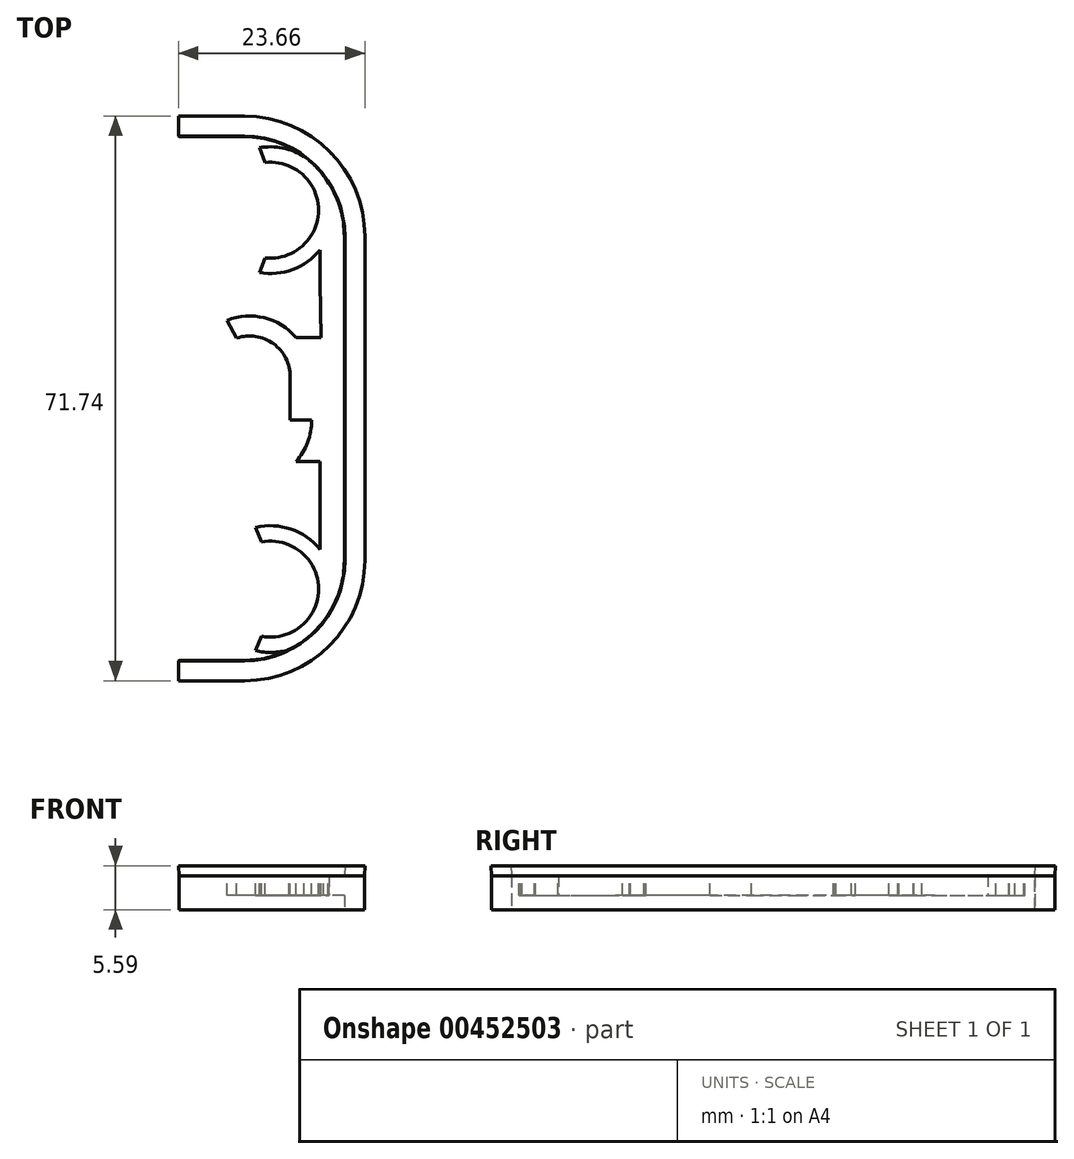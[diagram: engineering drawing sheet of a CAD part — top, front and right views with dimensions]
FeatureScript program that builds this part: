
annotation { "Feature Type Name" : "Feature", "Feature Type Description" : "" }
export const myFeature = defineFeature(function(context is Context, id is Id, definition is map)
    precondition{}
    {
        {
            var Q0;
            Q0=qCreatedBy(makeId("Top.planeOp"),FACE);
            var sketch = newSketch(context, id + "F0", { "sketchPlane" : qUnion([Q0])});
            skLineSegment(sketch, "E0", {"start": v(0, 0) * mm, "end": v(0, -66.52) * mm});
            skLineSegment(sketch, "E1", {"start": v(0, -66.52) * mm, "end": v(5.74, -66.52) * mm});
            skLineSegment(sketch, "E2", {"start": v(0, 0) * mm, "end": v(5.74, 0) * mm});
            skArc(sketch, "E3", {"start": v(5.74, 0) * mm, "mid": v(14.72, -3.72) * mm, "end": v(18.44, -12.7) * mm});
            skArc(sketch, "E4", {"start": v(5.74, -66.52) * mm, "mid": v(14.72, -62.8) * mm, "end": v(18.44, -53.82) * mm});
            skLineSegment(sketch, "E5", {"start": v(18.44, -12.7) * mm, "end": v(18.44, -53.82) * mm});
            skLineSegment(sketch, "E6.0", {"start": v(-2.54, 2.54) * mm, "end": v(5.74, 2.54) * mm});
            skLineSegment(sketch, "E6.1", {"start": v(20.98, -12.7) * mm, "end": v(20.98, -53.82) * mm});
            skArc(sketch, "E6.2", {"start": v(5.74, -69.06) * mm, "mid": v(16.52, -64.6) * mm, "end": v(20.98, -53.82) * mm});
            skArc(sketch, "E6.3", {"start": v(5.74, 2.54) * mm, "mid": v(16.52, -1.92) * mm, "end": v(20.98, -12.7) * mm});
            skLineSegment(sketch, "E6.4", {"start": v(-2.54, -69.06) * mm, "end": v(5.74, -69.06) * mm});
            skLineSegment(sketch, "E6.5", {"start": v(-2.54, 2.54) * mm, "end": v(-2.54, -69.06) * mm});
            skSolve(sketch);
        }
        {
            var Q0;
            Q0=makeQuery(id+"F0.imprint","IMPRINT",FACE,{"disambiguationData":[TD([[makeQuery(id+"F0.imprint","IMPRINT",EDGE,{"derivedFrom":sQuery(id+"F0.wireOp",EDGE,"E0")}),-1.0]])]});
            var Q1;
            Q1=makeQuery(id+"F0.imprint","IMPRINT",FACE,{"disambiguationData":[TD([[makeQuery(id+"F0.imprint","IMPRINT",EDGE,{"derivedFrom":sQuery(id+"F0.wireOp",EDGE,"E0")}),1.0]])]});
            extrude(context, id + "F1", {"entities" : qUnion([Q0, Q1]), "depth" : 1.27 * mm, "hasDraft" : true, "draftAngle" : 3 * degree, "hasSecondDirection" : true, "secondDirectionOppositeDirection" : true, "secondDirectionDepth" : 4.32 * mm});
        }
        {
            var Q0;
            Q0=makeQuery(id+"F1.opExtrude","CAP_FACE",FACE,{"disambiguationData":[OSD([sQuery(id+"F0.wireOp",EDGE,"E6.0"),sQuery(id+"F0.wireOp",EDGE,"E6.1"),sQuery(id+"F0.wireOp",EDGE,"E6.2"),sQuery(id+"F0.wireOp",EDGE,"E6.3"),sQuery(id+"F0.wireOp",EDGE,"E6.4"),sQuery(id+"F0.wireOp",EDGE,"E6.5")])],"isStart":false});
            var Q1;
            Q1=makeQuery(id+"F1.*.split.splitOp","SPLIT",FACE,{"derivedFrom":makeQuery(id+"F1.opExtrude","SWEPT_FACE",FACE,{"disambiguationData":[OSD([sQuery(id+"F0.wireOp",EDGE,"E6.5")])]})});
            var Q2;
            Q2=makeQuery(id+"F1.*.split.splitOp","SPLIT",FACE,{"derivedFrom":makeQuery(id+"F1.opExtrude","SWEPT_FACE",FACE,{"disambiguationData":[OSD([sQuery(id+"F0.wireOp",EDGE,"E6.5")])]}),"isFromBackBody":true});
            var Q3;
            Q3=makeQuery(id+"F1.opExtrude","CAP_FACE",FACE,{"disambiguationData":[OSD([sQuery(id+"F0.wireOp",EDGE,"E6.0"),sQuery(id+"F0.wireOp",EDGE,"E6.1"),sQuery(id+"F0.wireOp",EDGE,"E6.2"),sQuery(id+"F0.wireOp",EDGE,"E6.3"),sQuery(id+"F0.wireOp",EDGE,"E6.4"),sQuery(id+"F0.wireOp",EDGE,"E6.5")])],"isStart":true});
            shell(context, id + "F2", {"entities" : qUnion([Q0, Q1, Q2, Q3]), "thickness" : 2.54 * mm});
        }
        {
            var Q0;
            {var subQ0=sQuery(id+"F0.wireOp",EDGE,"E6.3");var subQ1=makeQuery(id+"F1.opExtrude","SWEPT_FACE",FACE,{"disambiguationData":[OSD([subQ0])]});var subQ2=sQuery(id+"F0.wireOp",EDGE,"E6.1");var subQ3=makeQuery(id+"F1.opExtrude","SWEPT_FACE",FACE,{"disambiguationData":[OSD([subQ2])]});Q0=makeQuery(id+"F2.opShell","OFFSET_VERTEX",VERTEX,{"disambiguationData":[OSD([subQ2,subQ0]),TDD([makeQuery(id+"F1.*.booleanUnion.opBoolean","MERGE",VERTEX,{"derivedFrom":[makeQuery(id+"F1.*.split.splitOp","SPLIT_SURFACE_INTERSECT",VERTEX,{"derivedFrom":[subQ3,subQ1]}),makeQuery(id+"F1.*.split.splitOp","SPLIT_SURFACE_INTERSECT",VERTEX,{"derivedFrom":[subQ3,subQ1],"isFromBackBody":true})]})])]});}
            var Q1;
            {var subQ0=sQuery(id+"F0.wireOp",EDGE,"E6.2");var subQ1=makeQuery(id+"F1.opExtrude","SWEPT_FACE",FACE,{"disambiguationData":[OSD([subQ0])]});var subQ2=sQuery(id+"F0.wireOp",EDGE,"E6.1");var subQ3=makeQuery(id+"F1.opExtrude","SWEPT_FACE",FACE,{"disambiguationData":[OSD([subQ2])]});Q1=makeQuery(id+"F2.opShell","OFFSET_VERTEX",VERTEX,{"disambiguationData":[OSD([subQ2,subQ0]),TDD([makeQuery(id+"F1.*.booleanUnion.opBoolean","MERGE",VERTEX,{"derivedFrom":[makeQuery(id+"F1.*.split.splitOp","SPLIT_SURFACE_INTERSECT",VERTEX,{"derivedFrom":[subQ3,subQ1]}),makeQuery(id+"F1.*.split.splitOp","SPLIT_SURFACE_INTERSECT",VERTEX,{"derivedFrom":[subQ3,subQ1],"isFromBackBody":true})]})])]});}
            var Q2;
            {var subQ0=sQuery(id+"F0.wireOp",EDGE,"E6.3");var subQ1=makeQuery(id+"F1.opExtrude","SWEPT_FACE",FACE,{"disambiguationData":[OSD([subQ0])]});var subQ2=sQuery(id+"F0.wireOp",EDGE,"E6.0");var subQ3=makeQuery(id+"F1.opExtrude","SWEPT_FACE",FACE,{"disambiguationData":[OSD([subQ2])]});Q2=makeQuery(id+"F2.opShell","OFFSET_VERTEX",VERTEX,{"disambiguationData":[OSD([subQ2,subQ0]),TDD([makeQuery(id+"F1.*.booleanUnion.opBoolean","MERGE",VERTEX,{"derivedFrom":[makeQuery(id+"F1.*.split.splitOp","SPLIT_SURFACE_INTERSECT",VERTEX,{"derivedFrom":[subQ3,subQ1]}),makeQuery(id+"F1.*.split.splitOp","SPLIT_SURFACE_INTERSECT",VERTEX,{"derivedFrom":[subQ3,subQ1],"isFromBackBody":true})]})])]});}
            cPlane(context, id + "F3", {"entities" : qUnion([Q0, Q1, Q2]), "cplaneType" : CPlaneType.THREE_POINT, "offset" : 25.4 * mm, "width" : 152.4 * mm, "height" : 152.4 * mm});
        }
        {
            var Q0;
            Q0=qCreatedBy(id+"F3.planeOp",FACE);
            var sketch = newSketch(context, id + "F4", { "sketchPlane" : qUnion([Q0])});
            skLineSegment(sketch, "E7", {"start": v(18.44, -36.02) * mm, "end": v(11.57, -36.02) * mm});
            skLineSegment(sketch, "E8", {"start": v(18.44, -30.5) * mm, "end": v(11.57, -30.5) * mm});
            skArc(sketch, "E9", {"start": v(11.57, -36.02) * mm, "mid": v(9.43, -40.21) * mm, "end": v(4.78, -40.94) * mm});
            skLineSegment(sketch, "E10", {"start": v(11.57, -36.02) * mm, "end": v(11.57, -30.5) * mm});
            skLineSegment(sketch, "E11", {"start": v(18.44, -36.02) * mm, "end": v(18.44, -30.5) * mm});
            skArc(sketch, "E12", {"start": v(11.57, -30.5) * mm, "mid": v(9.43, -26.31) * mm, "end": v(4.78, -25.58) * mm});
            skArc(sketch, "E13", {"start": v(14.1, -30.5) * mm, "mid": v(10.72, -24.11) * mm, "end": v(3.52, -23.34) * mm});
            skArc(sketch, "E14", {"start": v(14.3, -36.02) * mm, "mid": v(10.86, -42.55) * mm, "end": v(3.52, -43.4) * mm});
            skCircle(sketch, "E15", {"center": v(9.06, -9.35) * mm, "radius": 8.05 * mm});
            skCircle(sketch, "E16", {"center": v(9.06, -9.35) * mm, "radius": 6.1 * mm});
            skPoint(sketch, "E17.endSnap0", {"position": v(15.16, -9.35) * mm});
            skLineSegment(sketch, "E18", {"start": v(2.96, -9.35) * mm, "end": v(1, -9.35) * mm});
            skCircle(sketch, "E19", {"center": v(9.06, -57.48) * mm, "radius": 8.05 * mm});
            skCircle(sketch, "E20", {"center": v(9.06, -57.48) * mm, "radius": 6.1 * mm});
            skPoint(sketch, "E21.endSnap0", {"position": v(14.08, -57.48) * mm});
            skLineSegment(sketch, "E22", {"start": v(2.96, -57.48) * mm, "end": v(1, -57.48) * mm});
            skLineSegment(sketch, "E23", {"start": v(4.78, -25.58) * mm, "end": v(3.52, -23.34) * mm});
            skPoint(sketch, "E24", {"position": v(9.06, -22.67) * mm});
            skLineSegment(sketch, "E25", {"start": v(12.3, -25.53) * mm, "end": v(15.46, -25.53) * mm});
            skLineSegment(sketch, "E26", {"start": v(12.3, -41.29) * mm, "end": v(15.33, -41.29) * mm});
            skLineSegment(sketch, "E27", {"start": v(8.38, -15.4) * mm, "end": v(7.65, -17.27) * mm});
            skLineSegment(sketch, "E28", {"start": v(8.38, -3.29) * mm, "end": v(7.65, -1.42) * mm});
            skLineSegment(sketch, "E29", {"start": v(7.9, -63.46) * mm, "end": v(7.15, -65.3) * mm});
            skLineSegment(sketch, "E30", {"start": v(7.9, -51.5) * mm, "end": v(7.15, -49.66) * mm});
            skLineSegment(sketch, "E31", {"start": v(3.52, -43.4) * mm, "end": v(4.78, -40.94) * mm});
            skLineSegment(sketch, "E32", {"start": v(13.28, -64.13) * mm, "end": v(13.74, -64.03) * mm});
            skLineSegment(sketch, "E33.bottom", {"start": v(15.33, -30.5) * mm, "end": v(19.18, -30.5) * mm});
            skLineSegment(sketch, "E33.top", {"start": v(15.33, -5.97) * mm, "end": v(19.18, -5.97) * mm});
            skLineSegment(sketch, "E33.left", {"start": v(15.33, -30.5) * mm, "end": v(15.33, -5.97) * mm});
            skLineSegment(sketch, "E33.right", {"start": v(19.18, -30.5) * mm, "end": v(19.18, -5.97) * mm});
            skLineSegment(sketch, "E34.bottom", {"start": v(15.33, -36.02) * mm, "end": v(19.18, -36.02) * mm});
            skLineSegment(sketch, "E34.top", {"start": v(15.33, -60.55) * mm, "end": v(19.18, -60.55) * mm});
            skLineSegment(sketch, "E34.left", {"start": v(15.33, -36.02) * mm, "end": v(15.33, -60.55) * mm});
            skLineSegment(sketch, "E34.right", {"start": v(19.18, -36.02) * mm, "end": v(19.18, -60.55) * mm});
            skPoint(sketch, "E35", {"position": v(18.44, -33.26) * mm});
            skLineSegment(sketch, "E36", {"start": v(15.16, -9.35) * mm, "end": v(15.46, -25.53) * mm});
            skLineSegment(sketch, "E37", {"start": v(15.33, -41.29) * mm, "end": v(14.08, -57.48) * mm});
            skLineSegment(sketch, "E38", {"start": v(15.33, -41.29) * mm, "end": v(15.33, -57.48) * mm});
            skSolve(sketch);
        }
        {
            var Q0;
            {var subQ0=sQuery(id+"F4.wireOp",EDGE,"E27");Q0=makeQuery(id+"F4.imprint","IMPRINT",FACE,{"disambiguationData":[TD([[makeQuery(id+"F4.imprint","IMPRINT",EDGE,{"derivedFrom":subQ0}),1.0]])]});}
            var Q1;
            {var subQ0=sQuery(id+"F4.wireOp",EDGE,"E33.left");var subQ1=sQuery(id+"F4.wireOp",EDGE,"E15");var subQ2=makeQuery(id+"F4.imprint","INTERSECT",VERTEX,{"derivedFrom":[subQ1,subQ0]});Q1=makeQuery(id+"F4.imprint","IMPRINT",FACE,{"disambiguationData":[TD([[makeQuery(id+"F4.imprint","IMPRINT",EDGE,{"disambiguationData":[TD([[subQ2,-1.0]])],"derivedFrom":subQ1}),1.0]])]});}
            var Q2;
            {var subQ0=sQuery(id+"F4.wireOp",EDGE,"E27");Q2=makeQuery(id+"F4.imprint","IMPRINT",FACE,{"disambiguationData":[TD([[makeQuery(id+"F4.imprint","IMPRINT",EDGE,{"derivedFrom":subQ0}),1.0]])]});}
            var Q3;
            {var subQ3=sQuery(id+"F4.wireOp",EDGE,"E12");Q3=makeQuery(id+"F4.imprint","IMPRINT",FACE,{"disambiguationData":[TD([[makeQuery(id+"F4.imprint","IMPRINT",EDGE,{"derivedFrom":subQ3}),-1.0]])]});}
            var Q4;
            {var subQ5=sQuery(id+"F4.wireOp",EDGE,"E28");Q4=makeQuery(id+"F4.imprint","IMPRINT",FACE,{"disambiguationData":[TD([[makeQuery(id+"F4.imprint","IMPRINT",EDGE,{"derivedFrom":subQ5}),-1.0]])]});}
            var Q5;
            {var subQ0=sQuery(id+"F4.wireOp",EDGE,"E10");Q5=makeQuery(id+"F4.imprint","IMPRINT",FACE,{"disambiguationData":[TD([[makeQuery(id+"F4.imprint","IMPRINT",EDGE,{"derivedFrom":subQ0}),-1.0]])]});}
            var Q6;
            {var subQ4=sQuery(id+"F4.wireOp",EDGE,"E9");Q6=makeQuery(id+"F4.imprint","IMPRINT",FACE,{"disambiguationData":[TD([[makeQuery(id+"F4.imprint","IMPRINT",EDGE,{"derivedFrom":subQ4}),1.0]])]});}
            var Q7;
            {var subQ5=sQuery(id+"F4.wireOp",EDGE,"E26");Q7=makeQuery(id+"F4.imprint","IMPRINT",FACE,{"disambiguationData":[TD([[makeQuery(id+"F4.imprint","IMPRINT",EDGE,{"derivedFrom":subQ5}),1.0]])]});}
            var Q8;
            {var subQ5=sQuery(id+"F4.wireOp",EDGE,"E25");Q8=makeQuery(id+"F4.imprint","IMPRINT",FACE,{"disambiguationData":[TD([[makeQuery(id+"F4.imprint","IMPRINT",EDGE,{"derivedFrom":subQ5}),-1.0]])]});}
            var Q9;
            {var subQ0=sQuery(id+"F4.wireOp",EDGE,"E30");Q9=makeQuery(id+"F4.imprint","IMPRINT",FACE,{"disambiguationData":[TD([[makeQuery(id+"F4.imprint","IMPRINT",EDGE,{"derivedFrom":subQ0}),-1.0]])]});}
            var Q10;
            {var subQ0=sQuery(id+"F4.wireOp",EDGE,"E29");Q10=makeQuery(id+"F4.imprint","IMPRINT",FACE,{"disambiguationData":[TD([[makeQuery(id+"F4.imprint","IMPRINT",EDGE,{"derivedFrom":subQ0}),1.0]])]});}
            var Q11;
            {var subQ2=sQuery(id+"F4.wireOp",EDGE,"E33.right");Q11=makeQuery(id+"F4.imprint","IMPRINT",FACE,{"disambiguationData":[TD([[makeQuery(id+"F4.imprint","IMPRINT",EDGE,{"derivedFrom":subQ2}),1.0]])]});}
            var Q12;
            {var subQ0=sQuery(id+"F4.wireOp",EDGE,"E34.right");Q12=makeQuery(id+"F4.imprint","IMPRINT",FACE,{"disambiguationData":[TD([[makeQuery(id+"F4.imprint","IMPRINT",EDGE,{"derivedFrom":subQ0}),-1.0]])]});}
            var Q13;
            {var subQ0=sQuery(id+"F4.wireOp",EDGE,"E34.left");var subQ1=makeQuery(id+"F4.imprint","IMPRINT",VERTEX,{"derivedFrom":subQ0});Q13=makeQuery(id+"F4.imprint","IMPRINT",FACE,{"disambiguationData":[TD([[makeQuery(id+"F4.imprint","IMPRINT",EDGE,{"disambiguationData":[TD([[subQ1,1.0]])],"derivedFrom":subQ0}),1.0]])]});}
            var Q14;
            {var subQ0=sQuery(id+"F4.wireOp",EDGE,"E34.top");var subQ1=sQuery(id+"F4.wireOp",EDGE,"E19");var subQ2=makeQuery(id+"F4.imprint","INTERSECT",VERTEX,{"derivedFrom":[subQ1,subQ0]});Q14=makeQuery(id+"F4.imprint","IMPRINT",FACE,{"disambiguationData":[TD([[makeQuery(id+"F4.imprint","IMPRINT",EDGE,{"disambiguationData":[TD([[subQ2,-1.0]])],"derivedFrom":subQ1}),1.0]])]});}
            extrude(context, id + "F5", {"entities" : qUnion([Q0, Q1, Q2, Q3, Q4, Q5, Q6, Q7, Q8, Q9, Q10, Q11, Q12, Q13, Q14]), "operationType" : NewBodyOperationType.ADD, "oppositeDirection" : true, "depth" : 2.54 * mm});
        }
    });
